# Revit family: 3 Way Diverter for Thermostat 3 Outlet use_TOTO_TBV01102
name_source: partatom
category: 衛生器具
revit_build: Autodesk Revit 2018 (Build: 20181011_1500(x64)
units: mm (PartAtom-declared; Revit-internal decimal feet)

## family parameters
OmniClass タイトル = Sanitary, Laundry, and Cleaning Equipment
OmniClass 番号 = 23.45.00.00
パーツ タイプ = 標準
ロード時にボイドで切り取り = いいえ
丸型コネクタ寸法 = 直径を使用
作業面ベース = いいえ
共有 = いいえ
常に垂直 = はい
部屋計算ポイント = いいえ

## types (1)
- 3 Way Diverter for Thermostat 3 Outlet use_TOTO_TBV01102
    Finish = faucet_material
    Height = 135  [stored 0.442913 ft]
    Length = 72.2  [stored 0.236877 ft]
    TOTO AsiaOceania = TBV01102B
    TOTO AsiaOceania URL = http://asia.toto.com
    TOTO China = TBV01102B
    TOTO China URL = http://www.toto.com.cn
    TOTO India = TBV01102B
    TOTO India URL = https://in.toto.com
    TOTO Thailand = TBV01102T
    TOTO Thailand URL = https://th.toto.com
    TOTO USA = TBV01102U
    TOTO USA URL = https://www.totousa.com
    TOTO Vietnam = TBV01102B
    TOTO Vietnam URL = https://vn.toto.com
    TOTO Vietnam URL 02 = https://vn.toto.com
    Width = 135  [stored 0.442913 ft]
    タイプの説明 = Required Valve Unit for 3 Way Diverter With On-Off Valve(TBN1101B)/单柄暗装三向转换阀体(三种出水切换/开闭切换)(TBN1101B)需另购
    モデル = TBV01102
    製造元 = TOTO Ltd.
    説明 = 3 Way Diverter for Thermostat 3 Outlet use/单柄暗装三向转换面板(三种出水切换/开闭切换)

note: [stored X ft] marks values corroborated as IEEE doubles in the binary element streams (Revit-internal decimal feet)

## geometry (parser evidence)
native form markers: Blend x2, Sweep x1
no freeform markers — native parametric forms only
